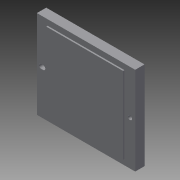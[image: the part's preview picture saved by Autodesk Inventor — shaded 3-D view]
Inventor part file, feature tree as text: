
AUTODESK INVENTOR PART (.ipt)
format: ipt  version: 2013 (Build 170138000, 138)  size: 101,376 bytes
history: native  units: in
note: dims shown in document units (in); Inventor stores cm internally (conversion verified against a paired STEP export)
features: sketch x3, extrude x2
ambient origin geometry x8: Origin, YZ Plane, XZ Plane, XY Plane, X Axis, Y Axis, Z Axis, Center Point
bodies: Solid1 (feature_tree)
feature tree (5):
  extrude  "Extrusion1"  Depth=1.6732in
  extrude  "Extrusion2"  Depth=0.0689in
  sketch  "Sketch3"  dims[d6=0.072in d7=0.1071in d8=1.4961in d9=0.1591in d10=0.0in d11=1.3079in d18=1.3079in d19=0.024in d20=0.0in d21=0.752in d23=0.561in]
  sketch  "Sketch1"  dims[d0=1.5in d2=1.6732in]
  sketch  "Sketch2"  dims[d3=0.0886in d4=0.0689in]
